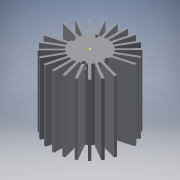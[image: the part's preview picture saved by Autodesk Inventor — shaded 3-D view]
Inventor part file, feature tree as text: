
AUTODESK INVENTOR PART (.ipt)
format: ipt  version: 2018 (Build 220112000, 112)  size: 391,680 bytes
history: native  units: mm
features: sketch x6, extrude x4, reference x2, other x2
ambient origin geometry x8: Origin, YZ Plane, XZ Plane, XY Plane, X Axis, Y Axis, Z Axis, Center Point
bodies: Solid1 (feature_tree)
feature tree (14):
  extrude  "Extrusion1"  Depth=40.0mm TaperAngle=0.0deg
  extrude  "Extrusion2"  Depth=2.43mm
  extrude  "Extrusion3"  Depth=40.0mm
  sketch  "Sketch5"  dims[d8=11.44mm d9=11.44mm]
  sketch  "Sketch9"  dims[d10=0.65mm]
  extrude  "Extrusion6"  Depth=11.44mm
  sketch  "Sketch1"  dims[d0=19.91mm d1=40.0mm d2=0.0mm]
  sketch  "Sketch2"  dims[d3=2.43mm d4=2.43mm]
  sketch  "Sketch3"  dims[d5=40.0mm d6=0.0mm d7=42.0116mm]
  sketch  "Sketch10"  dims[d11=0.65mm d12=40.0mm d13=0.0mm d14=110.0mm d16=25.900686mm d18=0.65mm d19=0.65mm d20=110.0mm d22=25.900686mm d38=6.0mm d39=0.0mm]
  reference  "Reference4"
  reference  "Reference5"
  other  "Assembly1"
  other  "M850D2:1"
